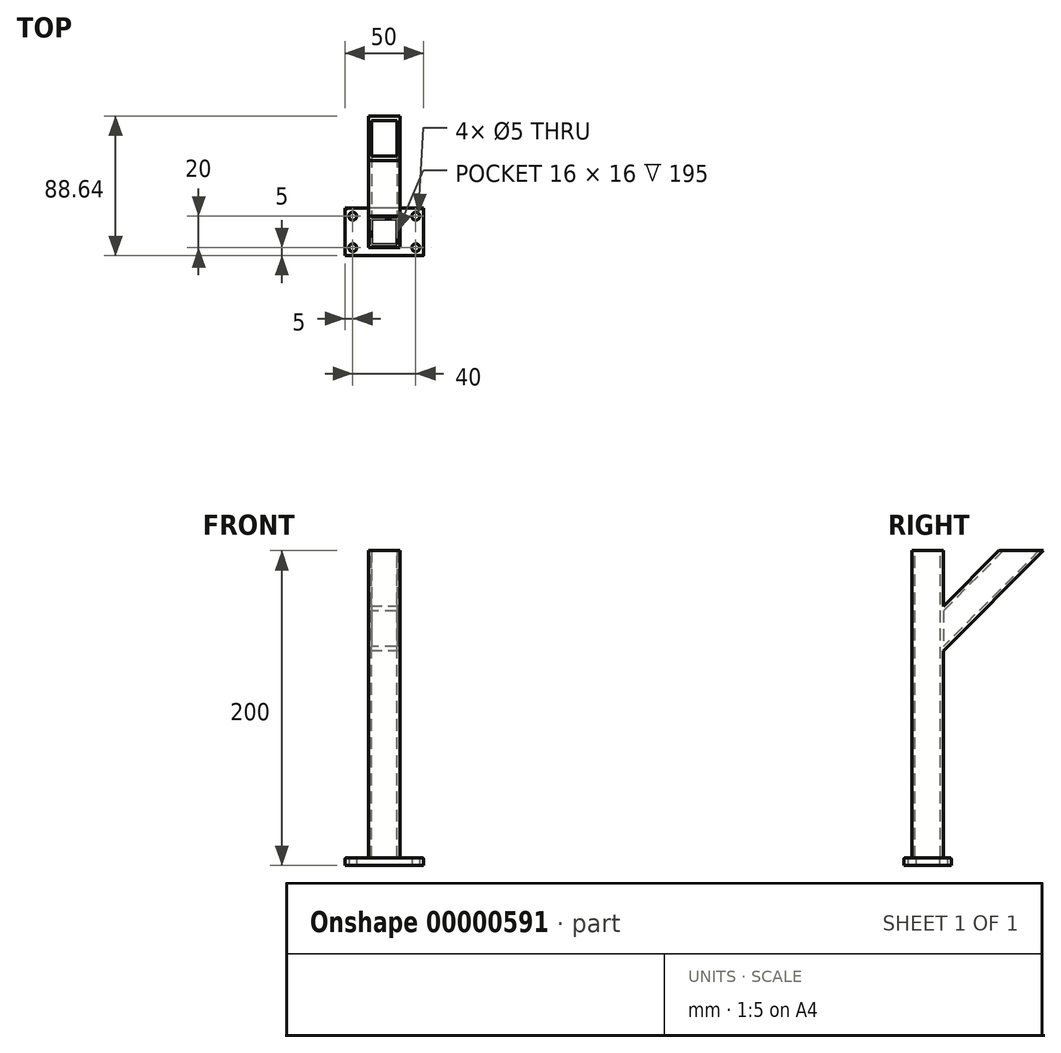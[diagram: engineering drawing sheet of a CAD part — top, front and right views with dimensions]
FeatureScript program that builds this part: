
annotation { "Feature Type Name" : "Feature", "Feature Type Description" : "" }
export const myFeature = defineFeature(function(context is Context, id is Id, definition is map)
    precondition{}
    {
        {
            var Q0;
            Q0 = qCreatedBy(makeId("Top.planeOp"), FACE);
            var sketch = newSketch(context, id + "F0", { "sketchPlane" : qUnion([Q0])});
            skLineSegment(sketch, "E0.rect.bottom", {"start": v(10, 10) * mm, "end": v(-10, 10) * mm});
            skLineSegment(sketch, "E0.rect.top", {"start": v(10, -10) * mm, "end": v(-10, -10) * mm});
            skLineSegment(sketch, "E0.rect.left", {"start": v(10, 10) * mm, "end": v(10, -10) * mm});
            skLineSegment(sketch, "E0.rect.right", {"start": v(-10, 10) * mm, "end": v(-10, -10) * mm});
            skPoint(sketch, "E0.rect.middle", {"position": v(0, 0) * mm});
            skSolve(sketch);
        }
        {
            var Q0;
            Q0=makeQuery(id+"F0.imprint","IMPRINT",FACE,{"disambiguationData":[TD([[makeQuery(id+"F0.imprint","IMPRINT",EDGE,{"derivedFrom":sQuery(id+"F0.wireOp",EDGE,"E0.rect.bottom")}),1.0]])]});
            extrude(context, id + "F1", {"entities" : qUnion([Q0]), "oppositeDirection" : true, "depth" : 200 * mm});
        }
        {
            var Q0;
            Q0=makeQuery(id+"F1.opExtrude","CAP_FACE",FACE,{"disambiguationData":[OSD([sQuery(id+"F0.wireOp",EDGE,"E0.rect.bottom"),sQuery(id+"F0.wireOp",EDGE,"E0.rect.top"),sQuery(id+"F0.wireOp",EDGE,"E0.rect.left"),sQuery(id+"F0.wireOp",EDGE,"E0.rect.right")])],"isStart":true});
            var Q1;
            Q1=makeQuery(id+"F1.opExtrude","CAP_FACE",FACE,{"disambiguationData":[OSD([sQuery(id+"F0.wireOp",EDGE,"E0.rect.bottom"),sQuery(id+"F0.wireOp",EDGE,"E0.rect.top"),sQuery(id+"F0.wireOp",EDGE,"E0.rect.left"),sQuery(id+"F0.wireOp",EDGE,"E0.rect.right")])],"isStart":false});
            shell(context, id + "F2", {"entities" : qUnion([Q0, Q1]), "thickness" : 2 * mm});
        }
        {
            var Q0;
            Q0=makeQuery(id+"F1.opExtrude","CAP_FACE",FACE,{"disambiguationData":[OSD([sQuery(id+"F0.wireOp",EDGE,"E0.rect.bottom"),sQuery(id+"F0.wireOp",EDGE,"E0.rect.top"),sQuery(id+"F0.wireOp",EDGE,"E0.rect.left"),sQuery(id+"F0.wireOp",EDGE,"E0.rect.right")])],"isStart":false});
            var sketch = newSketch(context, id + "F3", { "sketchPlane" : qUnion([Q0])});
            skLineSegment(sketch, "E1.rect.bottom", {"start": v(25, 15) * mm, "end": v(-25, 15) * mm});
            skLineSegment(sketch, "E1.rect.top", {"start": v(25, -15) * mm, "end": v(-25, -15) * mm});
            skLineSegment(sketch, "E1.rect.left", {"start": v(25, 15) * mm, "end": v(25, -15) * mm});
            skLineSegment(sketch, "E1.rect.right", {"start": v(-25, 15) * mm, "end": v(-25, -15) * mm});
            skPoint(sketch, "E1.rect.middle", {"position": v(0, 0) * mm});
            skLineSegment(sketch, "E2.rect.bottom", {"start": v(-20, 10) * mm, "end": v(20, 10) * mm, "construction": true});
            skLineSegment(sketch, "E2.rect.top", {"start": v(-20, -10) * mm, "end": v(20, -10) * mm, "construction": true});
            skLineSegment(sketch, "E2.rect.left", {"start": v(-20, 10) * mm, "end": v(-20, -10) * mm, "construction": true});
            skLineSegment(sketch, "E2.rect.right", {"start": v(20, 10) * mm, "end": v(20, -10) * mm, "construction": true});
            skCircle(sketch, "E3", {"center": v(-20, 10) * mm, "radius": 2.5 * mm});
            skCircle(sketch, "E4", {"center": v(20, 10) * mm, "radius": 2.5 * mm});
            skCircle(sketch, "E5", {"center": v(20, -10) * mm, "radius": 2.5 * mm});
            skCircle(sketch, "E6", {"center": v(-20, -10) * mm, "radius": 2.5 * mm});
            skSolve(sketch);
        }
        {
            var Q0;
            {var subQ9=sQuery(id+"F0.wireOp",EDGE,"E0.rect.bottom");var subQ10=makeQuery(id+"F1.opExtrude","CAP_EDGE",EDGE,{"disambiguationData":[OSD([subQ9])],"isStart":false});var subQ11=makeQuery(id+"F3.imprint","IMPRINT",EDGE,{"derivedFrom":makeQuery(id+"F2.opShell","OFFSET_EDGE",EDGE,{"disambiguationData":[OSD([subQ9]),TDD([subQ10])]})});var subQ15=makeQuery(id+"F3.imprint","IMPRINT",EDGE,{"derivedFrom":subQ10});Q0=qUnion([makeQuery(id+"F3.imprint","IMPRINT",FACE,{"disambiguationData":[TD([[subQ11,-1.0]])]}),makeQuery(id+"F3.imprint","IMPRINT",FACE,{"disambiguationData":[TD([[subQ15,-1.0]])]}),makeQuery(id+"F3.imprint","IMPRINT",FACE,{"disambiguationData":[TD([[makeQuery(id+"F3.imprint","IMPRINT",EDGE,{"derivedFrom":sQuery(id+"F3.wireOp",EDGE,"E1.rect.bottom")}),1.0]])]})]);}
            extrude(context, id + "F4", {"entities" : qUnion([Q0]), "operationType" : NewBodyOperationType.ADD, "oppositeDirection" : true, "depth" : 5 * mm});
        }
        {
            var Q0;
            Q0=makeQuery(id+"F4.opExtrude","CAP_EDGE",EDGE,{"disambiguationData":[OSD([sQuery(id+"F3.wireOp",EDGE,"E1.rect.top")])],"isStart":false});
            var Q1;
            Q1=makeQuery(id+"F4.opExtrude","CAP_EDGE",EDGE,{"disambiguationData":[OSD([sQuery(id+"F3.wireOp",EDGE,"E1.rect.right")])],"isStart":false});
            var Q2;
            Q2=makeQuery(id+"F4.opExtrude","CAP_EDGE",EDGE,{"disambiguationData":[OSD([sQuery(id+"F3.wireOp",EDGE,"E1.rect.bottom")])],"isStart":false});
            var Q3;
            Q3=makeQuery(id+"F4.opExtrude","CAP_EDGE",EDGE,{"disambiguationData":[OSD([sQuery(id+"F3.wireOp",EDGE,"E1.rect.left")])],"isStart":false});
            var Q4;
            Q4=makeQuery(id+"F4.opExtrude","CAP_EDGE",EDGE,{"disambiguationData":[OSD([sQuery(id+"F3.wireOp",EDGE,"E4")])],"isStart":false});
            var Q5;
            Q5=makeQuery(id+"F4.opExtrude","CAP_EDGE",EDGE,{"disambiguationData":[OSD([sQuery(id+"F3.wireOp",EDGE,"E5")])],"isStart":false});
            var Q6;
            Q6=makeQuery(id+"F4.opExtrude","CAP_EDGE",EDGE,{"disambiguationData":[OSD([sQuery(id+"F3.wireOp",EDGE,"E3")])],"isStart":false});
            var Q7;
            Q7=makeQuery(id+"F4.opExtrude","CAP_EDGE",EDGE,{"disambiguationData":[OSD([sQuery(id+"F3.wireOp",EDGE,"E6")])],"isStart":false});
            fillet(context, id + "F5", {"entities" : qUnion([Q0, Q1, Q2, Q3, Q4, Q5, Q6, Q7]), "radius" : 1 * mm, "tangentPropagation" : true, "allowEdgeOverflow" : false});
        }
        {
            var Q0;
            Q0 = qCreatedBy(makeId("Top.planeOp"), FACE);
            var Q1;
            Q1=makeQuery(id+"F1.opExtrude","SWEPT_FACE",FACE,{"disambiguationData":[OSD([sQuery(id+"F0.wireOp",EDGE,"E0.rect.bottom")])]});
            cPlane(context, id + "F6", {"entities" : qUnion([Q0, Q1]), "cplaneType" : CPlaneType.MID_PLANE, "offset" : 150 * mm, "flipAlignment" : true, "width" : 150 * mm, "height" : 150 * mm});
        }
        {
            var Q0;
            Q0=qCreatedBy(id+"F6.planeOp",FACE);
            var sketch = newSketch(context, id + "F7", { "sketchPlane" : qUnion([Q0])});
            skLineSegment(sketch, "E7.rect.bottom", {"start": v(10, -52.07) * mm, "end": v(-10, -52.07) * mm});
            skLineSegment(sketch, "E7.rect.top", {"start": v(10, -32.07) * mm, "end": v(-10, -32.07) * mm});
            skLineSegment(sketch, "E7.rect.left", {"start": v(10, -52.07) * mm, "end": v(10, -32.07) * mm});
            skLineSegment(sketch, "E7.rect.right", {"start": v(-10, -52.07) * mm, "end": v(-10, -32.07) * mm});
            skPoint(sketch, "E7.rect.middle", {"position": v(0, -42.07) * mm});
            skSolve(sketch);
        }
        {
            var Q0;
            Q0=makeQuery(id+"F7.imprint","IMPRINT",FACE,{"disambiguationData":[TD([[makeQuery(id+"F7.imprint","IMPRINT",EDGE,{"derivedFrom":sQuery(id+"F7.wireOp",EDGE,"E7.rect.bottom")}),-1.0]])]});
            var Q1;
            Q1 = qCreatedBy(makeId("Top.planeOp"), FACE);
            extrude(context, id + "F8", {"entities" : qUnion([Q0]), "endBound" : BoundingType.UP_TO_SURFACE, "endBoundEntityFace" : qUnion([Q1]), "depth" : 25 * mm});
        }
        {
            var Q0;
            Q0=makeQuery(id+"F7.imprint","IMPRINT",FACE,{"disambiguationData":[TD([[makeQuery(id+"F7.imprint","IMPRINT",EDGE,{"derivedFrom":sQuery(id+"F7.wireOp",EDGE,"E7.rect.bottom")}),-1.0]])]});
            var Q1;
            Q1=makeQuery(id+"F1.opExtrude","SWEPT_FACE",FACE,{"disambiguationData":[OSD([sQuery(id+"F0.wireOp",EDGE,"E0.rect.bottom")])]});
            extrude(context, id + "F9", {"entities" : qUnion([Q0]), "operationType" : NewBodyOperationType.ADD, "endBound" : BoundingType.UP_TO_SURFACE, "oppositeDirection" : true, "endBoundEntityFace" : qUnion([Q1]), "depth" : 25 * mm});
        }
        {
            var Q0;
            Q0=makeQuery(id+"F8.opExtrude","CAP_FACE",FACE,{"disambiguationData":[OSD([sQuery(id+"F7.wireOp",EDGE,"E7.rect.bottom"),sQuery(id+"F7.wireOp",EDGE,"E7.rect.top"),sQuery(id+"F7.wireOp",EDGE,"E7.rect.left"),sQuery(id+"F7.wireOp",EDGE,"E7.rect.right")])],"isStart":false});
            shell(context, id + "F10", {"entities" : qUnion([Q0]), "thickness" : 2 * mm});
        }
    });
